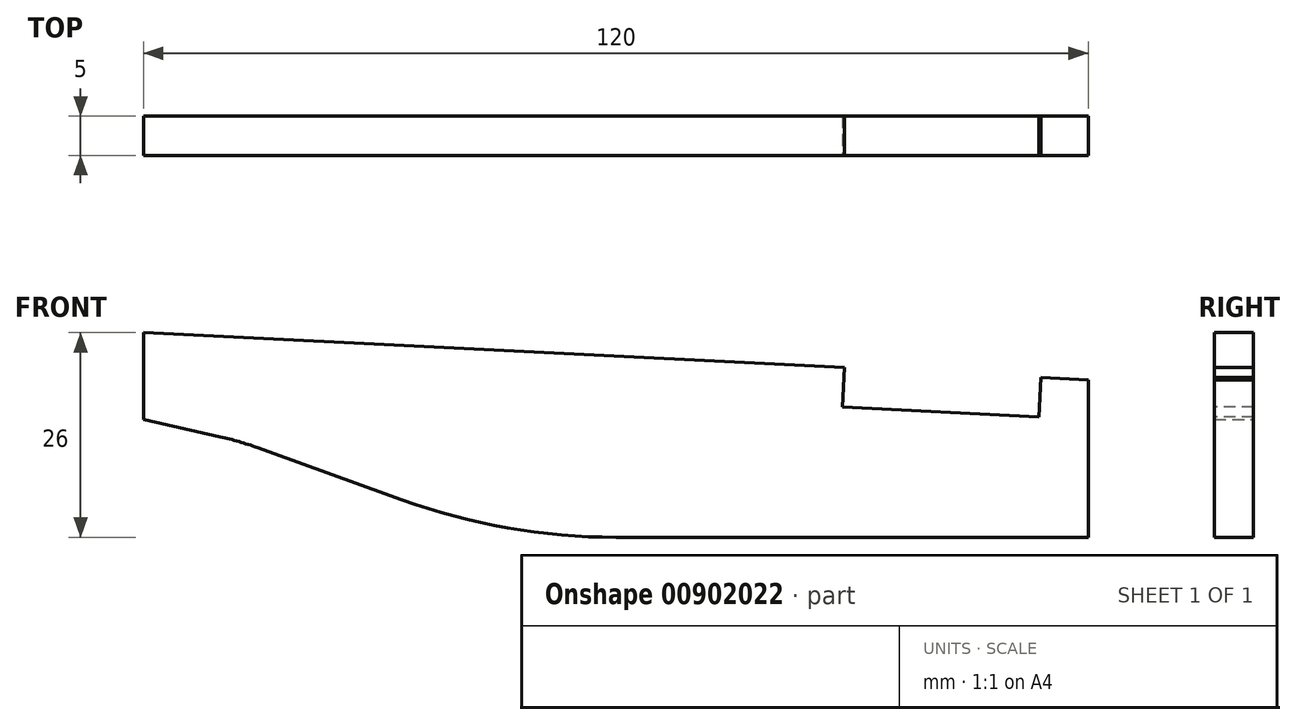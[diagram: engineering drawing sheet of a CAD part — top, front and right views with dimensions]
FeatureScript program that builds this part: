
annotation { "Feature Type Name" : "Feature", "Feature Type Description" : "" }
export const myFeature = defineFeature(function(context is Context, id is Id, definition is map)
    precondition{}
    {
        {
            var Q0;
            Q0=qCreatedBy(makeId("Front.planeOp"),FACE);
            var sketch = newSketch(context, id + "F0", { "sketchPlane" : qUnion([Q0])});
            skLineSegment(sketch, "E0.bottom", {"start": v(-120, 26) * mm, "end": v(0, 20) * mm});
            skLineSegment(sketch, "E0.top", {"start": v(-60, 0) * mm, "end": v(0, 0) * mm});
            skLineSegment(sketch, "E0.left", {"start": v(0, 20) * mm, "end": v(0, 0) * mm});
            skLineSegment(sketch, "E0.right", {"start": v(-120, 26) * mm, "end": v(-120, 15) * mm});
            skArc(sketch, "E1", {"start": v(-87.17, 4.76) * mm, "mid": v(-73.8, 1.2) * mm, "end": v(-60, 0) * mm});
            skLineSegment(sketch, "E2", {"start": v(-87.17, 4.76) * mm, "end": v(-105.57, 11.4) * mm});
            skLineSegment(sketch, "E3", {"start": v(-120, 15) * mm, "end": v(-110.25, 12.77) * mm});
            skArc(sketch, "E4", {"start": v(-105.57, 11.4) * mm, "mid": v(-107.89, 12.16) * mm, "end": v(-110.25, 12.77) * mm});
            skSolve(sketch);
        }
        {
            var Q0;
            Q0 = qSketchRegion(id + "F0", true);
            extrude(context, id + "F1", {"entities" : qUnion([Q0]), "depth" : 5 * mm, "offsetDistance" : 25 * mm});
        }
        {
            var Q0;
            Q0=makeQuery(id+"F1.opExtrude","CAP_FACE",FACE,{"disambiguationData":[OSD([sQuery(id+"F0.wireOp",EDGE,"E0.bottom"),sQuery(id+"F0.wireOp",EDGE,"E0.top"),sQuery(id+"F0.wireOp",EDGE,"E0.left"),sQuery(id+"F0.wireOp",EDGE,"E0.right"),sQuery(id+"F0.wireOp",EDGE,"E1"),sQuery(id+"F0.wireOp",EDGE,"E2"),sQuery(id+"F0.wireOp",EDGE,"E3"),sQuery(id+"F0.wireOp",EDGE,"E4")])],"isStart":false});
            var sketch = newSketch(context, id + "F2", { "sketchPlane" : qUnion([Q0])});
            skLineSegment(sketch, "E5.bottom", {"start": v(-6, 20.3) * mm, "end": v(-30.96, 21.55) * mm});
            skLineSegment(sketch, "E5.top", {"start": v(-6.24, 15.3) * mm, "end": v(-31.21, 16.55) * mm});
            skLineSegment(sketch, "E5.left", {"start": v(-6, 20.3) * mm, "end": v(-6.24, 15.3) * mm});
            skLineSegment(sketch, "E5.right", {"start": v(-30.96, 21.55) * mm, "end": v(-31.21, 16.55) * mm});
            skSolve(sketch);
        }
        {
            var Q0;
            Q0 = qSketchRegion(id + "F2", true);
            extrude(context, id + "F3", {"entities" : qUnion([Q0]), "operationType" : NewBodyOperationType.REMOVE, "oppositeDirection" : true, "depth" : 25 * mm, "offsetDistance" : 25 * mm});
        }
    });
